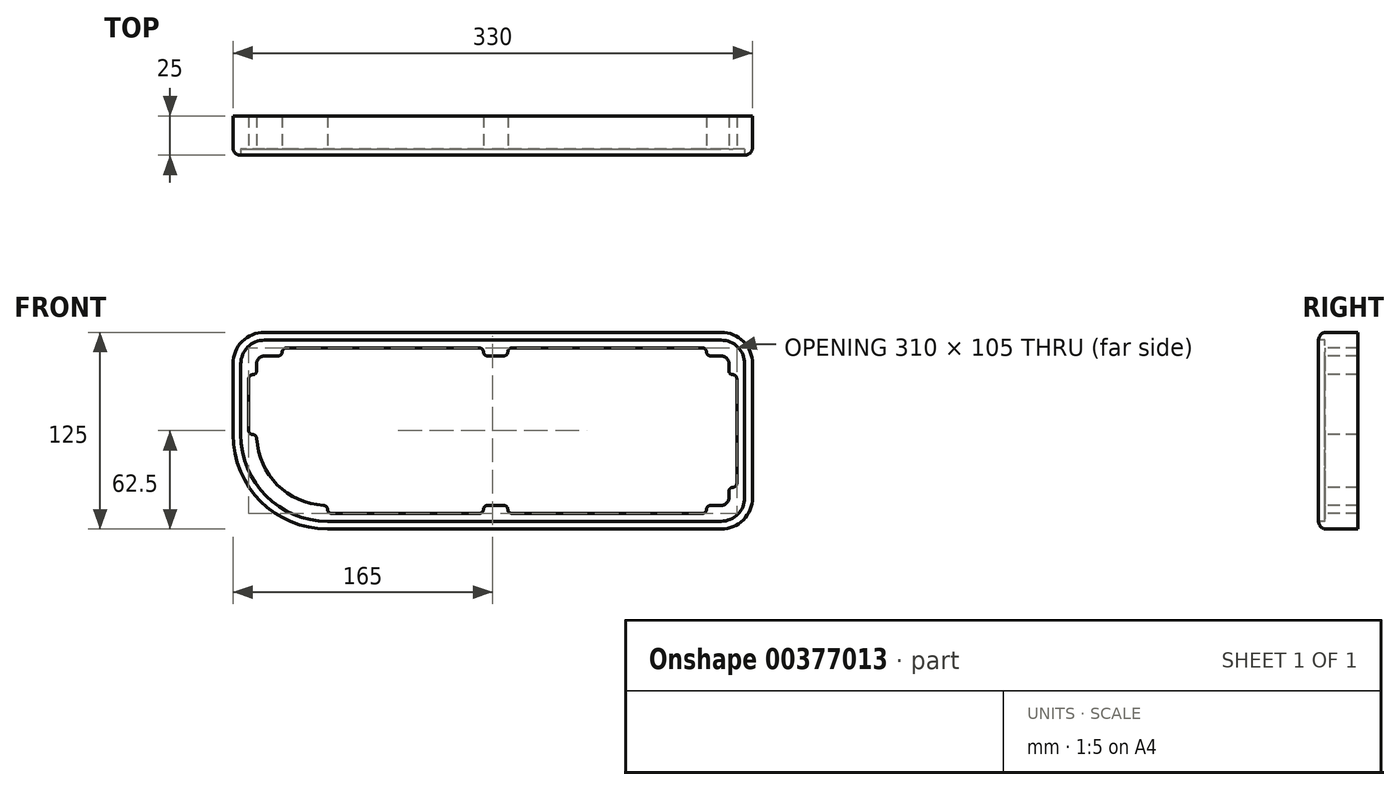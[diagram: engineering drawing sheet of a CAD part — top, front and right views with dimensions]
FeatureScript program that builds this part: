
annotation { "Feature Type Name" : "Feature", "Feature Type Description" : "" }
export const myFeature = defineFeature(function(context is Context, id is Id, definition is map)
    precondition{}
    {
        {
            var Q0;
            Q0=qCreatedBy(makeId("Front.planeOp"),FACE);
            var sketch = newSketch(context, id + "F0", { "sketchPlane" : qUnion([Q0])});
            skLineSegment(sketch, "E0.bottom", {"start": v(55, 0) * mm, "end": v(305, 0) * mm});
            skLineSegment(sketch, "E0.top", {"start": v(15, 115) * mm, "end": v(305, 115) * mm});
            skLineSegment(sketch, "E0.left", {"start": v(0, 55) * mm, "end": v(0, 100) * mm});
            skLineSegment(sketch, "E0.right", {"start": v(320, 15) * mm, "end": v(320, 100) * mm});
            skPoint(sketch, "E1.visualSharp", {"position": v(0, 115) * mm});
            skArc(sketch, "E1.filletArc", {"start": v(15, 115) * mm, "mid": v(4.4, 110.6) * mm, "end": v(0, 100) * mm});
            skPoint(sketch, "E2.visualSharp", {"position": v(320, 115) * mm});
            skArc(sketch, "E2.filletArc", {"start": v(320, 100) * mm, "mid": v(315.6, 110.6) * mm, "end": v(305, 115) * mm});
            skPoint(sketch, "E3.visualSharp", {"position": v(320, 0) * mm});
            skArc(sketch, "E3.filletArc", {"start": v(305, 0) * mm, "mid": v(315.6, 4.4) * mm, "end": v(320, 15) * mm});
            skPoint(sketch, "E4.visualSharp", {"position": v(0, 0) * mm});
            skArc(sketch, "E4.filletArc", {"start": v(0, 55) * mm, "mid": v(16.1, 16.1) * mm, "end": v(55, 0) * mm});
            skArc(sketch, "E5.0", {"start": v(15, 120) * mm, "mid": v(0.86, 114.14) * mm, "end": v(-5, 100) * mm});
            skLineSegment(sketch, "E5.1", {"start": v(-5, 55) * mm, "end": v(-5, 100) * mm});
            skLineSegment(sketch, "E5.2", {"start": v(15, 120) * mm, "end": v(305, 120) * mm});
            skArc(sketch, "E5.3", {"start": v(-5, 55) * mm, "mid": v(12.57, 12.57) * mm, "end": v(55, -5) * mm});
            skArc(sketch, "E5.4", {"start": v(325, 100) * mm, "mid": v(319.14, 114.14) * mm, "end": v(305, 120) * mm});
            skLineSegment(sketch, "E5.5", {"start": v(325, 15) * mm, "end": v(325, 100) * mm});
            skArc(sketch, "E5.6", {"start": v(305, -5) * mm, "mid": v(319.14, 0.86) * mm, "end": v(325, 15) * mm});
            skLineSegment(sketch, "E5.7", {"start": v(55, -5) * mm, "end": v(305, -5) * mm});
            skLineSegment(sketch, "E6", {"start": v(160, 115) * mm, "end": v(164.05, 0) * mm});
            skLineSegment(sketch, "E7", {"start": v(189.87, 0) * mm, "end": v(186.97, 115) * mm});
            skPoint(sketch, "E8.direction1.start.orphan", {"position": v(300, 20) * mm});
            skSolve(sketch);
        }
        {
            var Q0;
            Q0=qCreatedBy(makeId("Front.planeOp"),FACE);
            var sketch = newSketch(context, id + "F1", { "sketchPlane" : qUnion([Q0])});
            skLineSegment(sketch, "E9.0", {"start": v(-5, 55) * mm, "end": v(-5, 100) * mm});
            skArc(sketch, "E10.0", {"start": v(15, 120) * mm, "mid": v(0.86, 114.14) * mm, "end": v(-5, 100) * mm});
            skArc(sketch, "E11.0", {"start": v(-5, 55) * mm, "mid": v(12.57, 12.57) * mm, "end": v(55, -5) * mm});
            skLineSegment(sketch, "E12.0", {"start": v(55, -5) * mm, "end": v(305, -5) * mm});
            skLineSegment(sketch, "E13.0", {"start": v(15, 120) * mm, "end": v(305, 120) * mm});
            skPoint(sketch, "E14.0", {"position": v(320, 115) * mm});
            skPoint(sketch, "E15.0", {"position": v(319.14, 114.14) * mm});
            skArc(sketch, "E16.0", {"start": v(325, 100) * mm, "mid": v(319.14, 114.14) * mm, "end": v(305, 120) * mm});
            skLineSegment(sketch, "E17.0", {"start": v(325, 15) * mm, "end": v(325, 100) * mm});
            skArc(sketch, "E18.0", {"start": v(305, -5) * mm, "mid": v(319.14, 0.86) * mm, "end": v(325, 15) * mm});
            skLineSegment(sketch, "E19.0.5", {"start": v(305, 120) * mm, "end": v(15, 120) * mm});
            skLineSegment(sketch, "E19.0.7", {"start": v(-5, 100) * mm, "end": v(-5, 55) * mm});
            skSolve(sketch);
        }
        {
            var Q0;
            Q0=makeQuery(id+"F1.imprint","IMPRINT",FACE,{"disambiguationData":[TD([[makeQuery(id+"F1.imprint","IMPRINT",EDGE,{"derivedFrom":sQuery(id+"F1.wireOp",EDGE,"E11.0")}),1.0]])]});
            extrude(context, id + "F2", {"entities" : qUnion([Q0]), "depth" : 25 * mm});
        }
        {
            var Q0;
            Q0=makeQuery(id+"F2.opExtrude","CAP_EDGE",EDGE,{"disambiguationData":[OSD([sQuery(id+"F1.wireOp",EDGE,"E19.0.5")])],"isStart":false});
            var Q1;
            Q1=makeQuery(id+"F2.opExtrude","CAP_EDGE",EDGE,{"disambiguationData":[OSD([sQuery(id+"F1.wireOp",EDGE,"E10.0")])],"isStart":false});
            var Q2;
            Q2=makeQuery(id+"F2.opExtrude","CAP_EDGE",EDGE,{"disambiguationData":[OSD([sQuery(id+"F1.wireOp",EDGE,"E19.0.7")])],"isStart":false});
            var Q3;
            Q3=makeQuery(id+"F2.opExtrude","CAP_EDGE",EDGE,{"disambiguationData":[OSD([sQuery(id+"F1.wireOp",EDGE,"E11.0")])],"isStart":false});
            var Q4;
            Q4=makeQuery(id+"F2.opExtrude","CAP_EDGE",EDGE,{"disambiguationData":[OSD([sQuery(id+"F1.wireOp",EDGE,"E12.0")])],"isStart":false});
            var Q5;
            Q5=makeQuery(id+"F2.opExtrude","CAP_EDGE",EDGE,{"disambiguationData":[OSD([sQuery(id+"F1.wireOp",EDGE,"E18.0")])],"isStart":false});
            var Q6;
            Q6=makeQuery(id+"F2.opExtrude","CAP_EDGE",EDGE,{"disambiguationData":[OSD([sQuery(id+"F1.wireOp",EDGE,"E17.0")])],"isStart":false});
            var Q7;
            Q7=makeQuery(id+"F2.opExtrude","CAP_EDGE",EDGE,{"disambiguationData":[OSD([sQuery(id+"F1.wireOp",EDGE,"E16.0")])],"isStart":false});
            fillet(context, id + "F3", {"entities" : qUnion([Q0, Q1, Q2, Q3, Q4, Q5, Q6, Q7]), "radius" : 5 * mm, "tangentPropagation" : true, "allowEdgeOverflow" : false});
        }
        {
            var Q0;
            Q0=makeQuery(id+"F2.opExtrude","CAP_FACE",FACE,{"disambiguationData":[OSD([sQuery(id+"F1.wireOp",EDGE,"E11.0"),sQuery(id+"F1.wireOp",EDGE,"E12.0"),sQuery(id+"F1.wireOp",EDGE,"E18.0"),sQuery(id+"F1.wireOp",EDGE,"E17.0"),sQuery(id+"F1.wireOp",EDGE,"E16.0"),sQuery(id+"F1.wireOp",EDGE,"E19.0.5"),sQuery(id+"F1.wireOp",EDGE,"E10.0"),sQuery(id+"F1.wireOp",EDGE,"E19.0.7")])],"isStart":false});
            var Q1;
            Q1=makeQuery(id+"F0.imprint","IMPRINT",FACE,{"disambiguationData":[TD([[makeQuery(id+"F0.imprint","IMPRINT",EDGE,{"derivedFrom":sQuery(id+"F0.wireOp",EDGE,"E0.right")}),1.0]])]});
            var Q2;
            Q2=makeQuery(id+"F2.opExtrude","CAP_FACE",FACE,{"disambiguationData":[OSD([sQuery(id+"F1.wireOp",EDGE,"E11.0"),sQuery(id+"F1.wireOp",EDGE,"E12.0"),sQuery(id+"F1.wireOp",EDGE,"E18.0"),sQuery(id+"F1.wireOp",EDGE,"E17.0"),sQuery(id+"F1.wireOp",EDGE,"E16.0"),sQuery(id+"F1.wireOp",EDGE,"E19.0.5"),sQuery(id+"F1.wireOp",EDGE,"E10.0"),sQuery(id+"F1.wireOp",EDGE,"E19.0.7")])],"isStart":true});
            extrude(context, id + "F4", {"entities" : qUnion([Q0, Q1, Q2]), "operationType" : NewBodyOperationType.REMOVE, "oppositeDirection" : true, "depth" : 4 * mm});
        }
        {
            var Q0;
            {var subQ0=sQuery(id+"F1.wireOp",EDGE,"E19.0.7");var subQ1=sQuery(id+"F1.wireOp",EDGE,"E10.0");var subQ2=sQuery(id+"F1.wireOp",EDGE,"E19.0.5");var subQ3=sQuery(id+"F1.wireOp",EDGE,"E16.0");var subQ4=sQuery(id+"F1.wireOp",EDGE,"E17.0");var subQ5=sQuery(id+"F1.wireOp",EDGE,"E18.0");var subQ6=sQuery(id+"F1.wireOp",EDGE,"E12.0");var subQ7=sQuery(id+"F1.wireOp",EDGE,"E11.0");Q0=makeQuery(id+"F4.boolean.opBoolean","COPY",FACE,{"derivedFrom":makeQuery(id+"F4.opExtrude","CAP_FACE",FACE,{"disambiguationData":[OSD([subQ7,subQ6,subQ5,subQ4,subQ3,subQ2,subQ1,subQ0]),TDD([makeQuery(id+"F2.opExtrude","CAP_FACE",FACE,{"disambiguationData":[OSD([subQ7,subQ6,subQ5,subQ4,subQ3,subQ2,subQ1,subQ0])],"isStart":false})])],"isStart":false})});}
            var sketch = newSketch(context, id + "F5", { "sketchPlane" : qUnion([Q0])});
            skArc(sketch, "E20.0.5", {"start": v(0, 55) * mm, "mid": v(16.1, 16.1) * mm, "end": v(55, 0) * mm});
            skArc(sketch, "E21.0", {"start": v(305, 10) * mm, "mid": v(308.54, 11.46) * mm, "end": v(310, 15) * mm});
            skLineSegment(sketch, "E21.1", {"start": v(156.6, 10) * mm, "end": v(167.06, 10) * mm});
            skLineSegment(sketch, "E21.2", {"start": v(310, 15) * mm, "end": v(310, 19.03) * mm});
            skArc(sketch, "E21.3", {"start": v(10.06, 52.63) * mm, "mid": v(23.18, 23.18) * mm, "end": v(52.63, 10.06) * mm});
            skArc(sketch, "E21.4", {"start": v(310, 100) * mm, "mid": v(308.54, 103.54) * mm, "end": v(305, 105) * mm});
            skLineSegment(sketch, "E21.5", {"start": v(305, 105) * mm, "end": v(298.29, 105) * mm});
            skArc(sketch, "E21.6", {"start": v(15, 105) * mm, "mid": v(11.46, 103.54) * mm, "end": v(10, 100) * mm});
            skLineSegment(sketch, "E21.7", {"start": v(10, 100) * mm, "end": v(10, 95.55) * mm});
            skPoint(sketch, "E20.0.3.start.orphan", {"position": v(15, 115) * mm});
            skPoint(sketch, "E20.0.4.start.orphan", {"position": v(0, 100) * mm});
            skPoint(sketch, "E20.0.1.end.orphan", {"position": v(305, 115) * mm});
            skPoint(sketch, "E20.0.0.end.orphan", {"position": v(320, 100) * mm});
            skPoint(sketch, "E20.0.7.end.orphan", {"position": v(320, 15) * mm});
            skPoint(sketch, "E20.0.6.end.orphan", {"position": v(305, 0) * mm});
            skLineSegment(sketch, "E22.1", {"start": v(315, 24.03) * mm, "end": v(315, 90.55) * mm});
            skLineSegment(sketch, "E22.2", {"start": v(293.29, 110) * mm, "end": v(172.06, 110) * mm});
            skLineSegment(sketch, "E22.5", {"start": v(5, 90.55) * mm, "end": v(5, 57.5) * mm});
            skLineSegment(sketch, "E22.7", {"start": v(57.5, 5) * mm, "end": v(151.6, 5) * mm});
            skLineSegment(sketch, "E23", {"start": v(295.79, 107.5) * mm, "end": v(295.79, 107.5) * mm});
            skLineSegment(sketch, "E24", {"start": v(169.56, 107.5) * mm, "end": v(169.56, 107.5) * mm});
            skLineSegment(sketch, "E25", {"start": v(154.1, 107.5) * mm, "end": v(154.1, 107.5) * mm});
            skLineSegment(sketch, "E26", {"start": v(26.27, 107.5) * mm, "end": v(26.27, 107.5) * mm});
            skLineSegment(sketch, "E27", {"start": v(7.5, 93.05) * mm, "end": v(7.5, 93.05) * mm});
            skLineSegment(sketch, "E28", {"start": v(7.57, 55) * mm, "end": v(7.5, 55) * mm});
            skLineSegment(sketch, "E29", {"start": v(55, 7.57) * mm, "end": v(55, 7.5) * mm});
            skLineSegment(sketch, "E30", {"start": v(154.1, 7.5) * mm, "end": v(154.1, 7.5) * mm});
            skLineSegment(sketch, "E31", {"start": v(169.56, 7.5) * mm, "end": v(169.56, 7.5) * mm});
            skLineSegment(sketch, "E32", {"start": v(295.79, 7.5) * mm, "end": v(295.79, 7.5) * mm});
            skLineSegment(sketch, "E33", {"start": v(312.5, 93.05) * mm, "end": v(312.5, 93.05) * mm});
            skLineSegment(sketch, "E34", {"start": v(312.5, 21.53) * mm, "end": v(312.5, 21.53) * mm});
            skLineSegment(sketch, "E35.trimOffspring", {"start": v(23.77, 105) * mm, "end": v(15, 105) * mm});
            skLineSegment(sketch, "E36.trimOffspring", {"start": v(151.6, 110) * mm, "end": v(28.77, 110) * mm});
            skLineSegment(sketch, "E37.trimOffspring", {"start": v(167.06, 105) * mm, "end": v(156.6, 105) * mm});
            skLineSegment(sketch, "E38.trimOffspring", {"start": v(310, 95.55) * mm, "end": v(310, 100) * mm});
            skLineSegment(sketch, "E39.trimOffspring", {"start": v(298.29, 10) * mm, "end": v(305, 10) * mm});
            skLineSegment(sketch, "E40.trimOffspring", {"start": v(172.06, 5) * mm, "end": v(293.29, 5) * mm});
            skPoint(sketch, "E41.visualSharp", {"position": v(10, 93.05) * mm});
            skArc(sketch, "E41.filletArc", {"start": v(7.5, 93.05) * mm, "mid": v(9.27, 93.78) * mm, "end": v(10, 95.55) * mm});
            skPoint(sketch, "E42.visualSharp", {"position": v(5, 93.05) * mm});
            skArc(sketch, "E42.filletArc", {"start": v(7.5, 93.05) * mm, "mid": v(5.73, 92.32) * mm, "end": v(5, 90.55) * mm});
            skPoint(sketch, "E43.visualSharp", {"position": v(26.27, 105) * mm});
            skArc(sketch, "E43.filletArc", {"start": v(23.77, 105) * mm, "mid": v(25.54, 105.73) * mm, "end": v(26.27, 107.5) * mm});
            skPoint(sketch, "E44.visualSharp", {"position": v(26.27, 110) * mm});
            skArc(sketch, "E44.filletArc", {"start": v(28.77, 110) * mm, "mid": v(27, 109.27) * mm, "end": v(26.27, 107.5) * mm});
            skPoint(sketch, "E45.visualSharp", {"position": v(5, 55) * mm});
            skArc(sketch, "E45.filletArc", {"start": v(5, 57.5) * mm, "mid": v(5.73, 55.73) * mm, "end": v(7.5, 55) * mm});
            skPoint(sketch, "E46.visualSharp", {"position": v(10, 55) * mm});
            skArc(sketch, "E46.filletArc", {"start": v(10.06, 52.63) * mm, "mid": v(9.29, 54.31) * mm, "end": v(7.57, 55) * mm});
            skPoint(sketch, "E47.visualSharp", {"position": v(55, 10) * mm});
            skArc(sketch, "E47.filletArc", {"start": v(55, 7.57) * mm, "mid": v(54.31, 9.29) * mm, "end": v(52.63, 10.06) * mm});
            skPoint(sketch, "E48.visualSharp", {"position": v(55, 5) * mm});
            skArc(sketch, "E48.filletArc", {"start": v(55, 7.5) * mm, "mid": v(55.73, 5.73) * mm, "end": v(57.5, 5) * mm});
            skPoint(sketch, "E49.visualSharp", {"position": v(154.1, 5) * mm});
            skArc(sketch, "E49.filletArc", {"start": v(151.6, 5) * mm, "mid": v(153.38, 5.73) * mm, "end": v(154.1, 7.5) * mm});
            skPoint(sketch, "E50.visualSharp", {"position": v(154.1, 10) * mm});
            skArc(sketch, "E50.filletArc", {"start": v(156.6, 10) * mm, "mid": v(154.84, 9.27) * mm, "end": v(154.1, 7.5) * mm});
            skPoint(sketch, "E51.visualSharp", {"position": v(169.56, 10) * mm});
            skArc(sketch, "E51.filletArc", {"start": v(169.56, 7.5) * mm, "mid": v(168.83, 9.27) * mm, "end": v(167.06, 10) * mm});
            skPoint(sketch, "E52.visualSharp", {"position": v(169.56, 5) * mm});
            skArc(sketch, "E52.filletArc", {"start": v(169.56, 7.5) * mm, "mid": v(170.3, 5.73) * mm, "end": v(172.06, 5) * mm});
            skPoint(sketch, "E53.visualSharp", {"position": v(295.79, 5) * mm});
            skArc(sketch, "E53.filletArc", {"start": v(293.29, 5) * mm, "mid": v(295.05, 5.73) * mm, "end": v(295.79, 7.5) * mm});
            skPoint(sketch, "E54.visualSharp", {"position": v(295.79, 10) * mm});
            skArc(sketch, "E54.filletArc", {"start": v(298.29, 10) * mm, "mid": v(296.52, 9.27) * mm, "end": v(295.79, 7.5) * mm});
            skPoint(sketch, "E55.visualSharp", {"position": v(310, 21.53) * mm});
            skArc(sketch, "E55.filletArc", {"start": v(312.5, 21.53) * mm, "mid": v(310.73, 20.8) * mm, "end": v(310, 19.03) * mm});
            skPoint(sketch, "E56.visualSharp", {"position": v(315, 21.53) * mm});
            skArc(sketch, "E56.filletArc", {"start": v(312.5, 21.53) * mm, "mid": v(314.27, 22.26) * mm, "end": v(315, 24.03) * mm});
            skPoint(sketch, "E57.visualSharp", {"position": v(315, 93.05) * mm});
            skArc(sketch, "E57.filletArc", {"start": v(315, 90.55) * mm, "mid": v(314.27, 92.32) * mm, "end": v(312.5, 93.05) * mm});
            skPoint(sketch, "E58.visualSharp", {"position": v(310, 93.05) * mm});
            skArc(sketch, "E58.filletArc", {"start": v(310, 95.55) * mm, "mid": v(310.73, 93.78) * mm, "end": v(312.5, 93.05) * mm});
            skPoint(sketch, "E59.visualSharp", {"position": v(295.79, 105) * mm});
            skArc(sketch, "E59.filletArc", {"start": v(295.79, 107.5) * mm, "mid": v(296.52, 105.73) * mm, "end": v(298.29, 105) * mm});
            skPoint(sketch, "E60.visualSharp", {"position": v(295.79, 110) * mm});
            skArc(sketch, "E60.filletArc", {"start": v(295.79, 107.5) * mm, "mid": v(295.05, 109.27) * mm, "end": v(293.29, 110) * mm});
            skPoint(sketch, "E61.visualSharp", {"position": v(169.56, 110) * mm});
            skArc(sketch, "E61.filletArc", {"start": v(172.06, 110) * mm, "mid": v(170.3, 109.27) * mm, "end": v(169.56, 107.5) * mm});
            skPoint(sketch, "E62.visualSharp", {"position": v(169.56, 105) * mm});
            skArc(sketch, "E62.filletArc", {"start": v(167.06, 105) * mm, "mid": v(168.83, 105.73) * mm, "end": v(169.56, 107.5) * mm});
            skPoint(sketch, "E63.visualSharp", {"position": v(154.1, 105) * mm});
            skArc(sketch, "E63.filletArc", {"start": v(154.1, 107.5) * mm, "mid": v(154.84, 105.73) * mm, "end": v(156.6, 105) * mm});
            skPoint(sketch, "E64.visualSharp", {"position": v(154.1, 110) * mm});
            skArc(sketch, "E64.filletArc", {"start": v(154.1, 107.5) * mm, "mid": v(153.38, 109.27) * mm, "end": v(151.6, 110) * mm});
            skSolve(sketch);
        }
        {
            var Q0;
            Q0=makeQuery(id+"F5.imprint","IMPRINT",FACE,{"disambiguationData":[TD([[makeQuery(id+"F5.imprint","IMPRINT",EDGE,{"derivedFrom":sQuery(id+"F5.wireOp",EDGE,"E21.0")}),1.0]])]});
            extrude(context, id + "F6", {"entities" : qUnion([Q0]), "operationType" : NewBodyOperationType.REMOVE, "oppositeDirection" : true, "depth" : 25 * mm});
        }
    });
